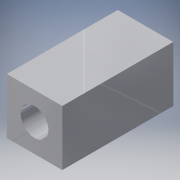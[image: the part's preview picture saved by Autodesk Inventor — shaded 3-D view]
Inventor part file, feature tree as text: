
AUTODESK INVENTOR PART (.ipt)
format: ipt  version: 2016 (Build 200138000, 138)  size: 93,184 bytes
history: native  units: in
note: dims shown in document units (in); Inventor stores cm internally (conversion verified against a paired STEP export)
features: extrude x1, sketch x1
ambient origin geometry x8: Origin, YZ Plane, XZ Plane, XY Plane, X Axis, Y Axis, Z Axis, Center Point
bodies: Solid1 (feature_tree)
feature tree (2):
  extrude  "Extrusion1"  Depth=0.5in
  sketch  "Sketch1"  dims[d0=0.25in d1=0.5in d2=0.5in d3=0.25in d4=0.25in d5=1.0in d6=0.0in]
